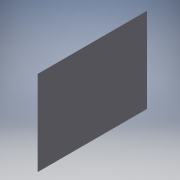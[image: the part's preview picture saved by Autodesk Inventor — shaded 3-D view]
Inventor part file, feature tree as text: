
AUTODESK INVENTOR PART (.ipt)
format: ipt  version: 2018 (Build 220112000, 112)  size: 94,208 bytes
history: native  units: mm
features: extrude x1, chamfer x1, sketch x1
ambient origin geometry x8: Origin, YZ Plane, XZ Plane, XY Plane, X Axis, Y Axis, Z Axis, Center Point
bodies: Volumenkörper1 (feature_tree)
feature tree (3):
  extrude  "Extrusion1"  Depth=20.0mm
  chamfer  "Fase1"  Distance=20.0mm
  sketch  "Skizze1"  dims[d0=400.0mm d1=450.0mm d2=20.0mm d3=0.0mm d4=20.0mm d5=2.0mm d6=45.0deg]
